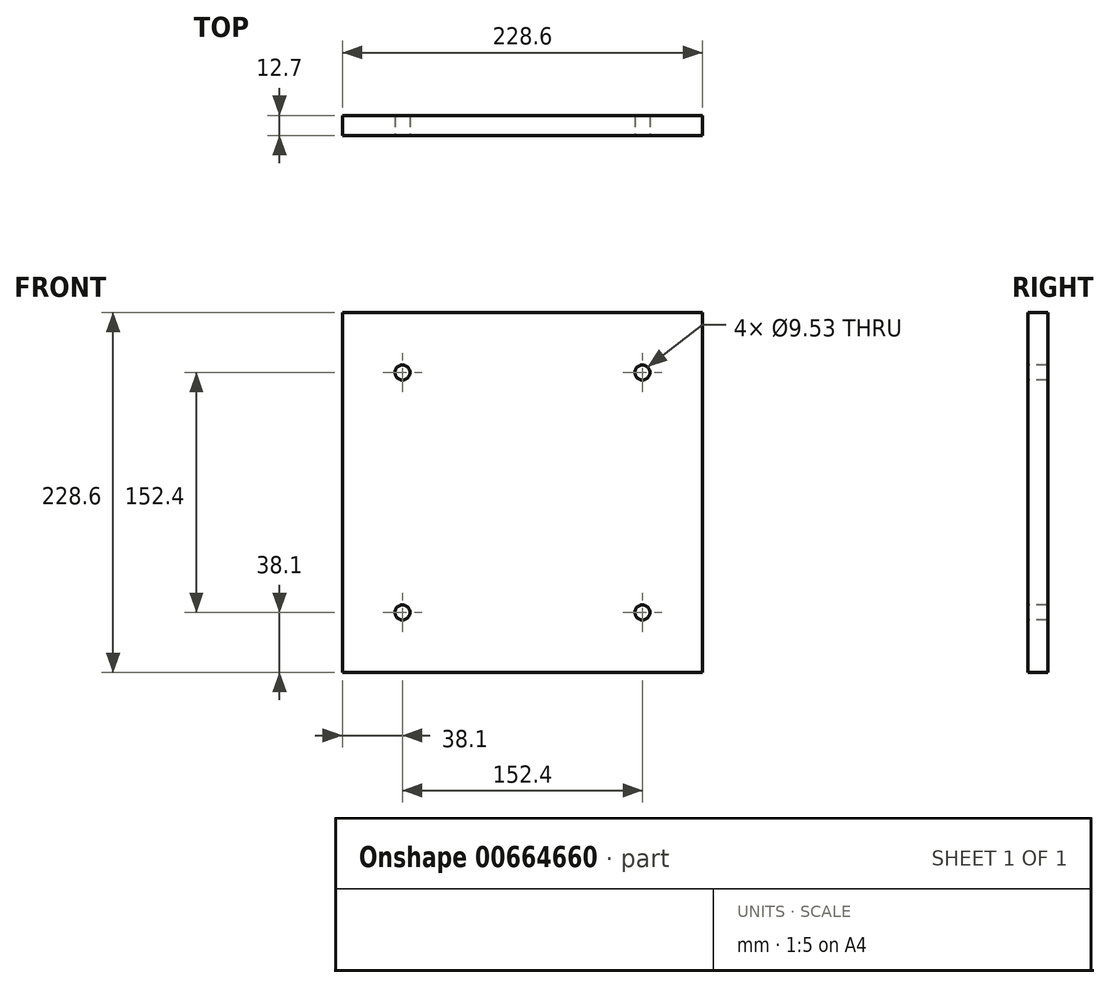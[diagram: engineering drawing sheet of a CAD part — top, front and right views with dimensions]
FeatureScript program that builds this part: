
annotation { "Feature Type Name" : "Feature", "Feature Type Description" : "" }
export const myFeature = defineFeature(function(context is Context, id is Id, definition is map)
    precondition{}
    {
        {
            var Q0;
            Q0=qCreatedBy(makeId("Front.planeOp"),FACE);
            var sketch = newSketch(context, id + "F0", { "sketchPlane" : qUnion([Q0])});
            skLineSegment(sketch, "E0.bottom", {"start": v(114.3, 114.3) * mm, "end": v(-114.3, 114.3) * mm});
            skLineSegment(sketch, "E0.top", {"start": v(114.3, -114.3) * mm, "end": v(-114.3, -114.3) * mm});
            skLineSegment(sketch, "E0.left", {"start": v(114.3, 114.3) * mm, "end": v(114.3, -114.3) * mm});
            skLineSegment(sketch, "E0.right", {"start": v(-114.3, 114.3) * mm, "end": v(-114.3, -114.3) * mm});
            skPoint(sketch, "E0.middle", {"position": v(0, 0) * mm});
            skSolve(sketch);
        }
        {
            var Q0;
            Q0 = qSketchRegion(id + "F0", true);
            extrude(context, id + "F1", {"entities" : qUnion([Q0]), "depth" : 12.7 * mm, "offsetDistance" : 25.4 * mm});
        }
        {
            var Q0;
            Q0=makeQuery(id+"F1.opExtrude","CAP_FACE",FACE,{"disambiguationData":[OSD([sQuery(id+"F0.wireOp",EDGE,"E0.bottom"),sQuery(id+"F0.wireOp",EDGE,"E0.top"),sQuery(id+"F0.wireOp",EDGE,"E0.left"),sQuery(id+"F0.wireOp",EDGE,"E0.right")])],"isStart":false});
            var sketch = newSketch(context, id + "F2", { "sketchPlane" : qUnion([Q0])});
            skLineSegment(sketch, "E1.bottom", {"start": v(76.2, 76.2) * mm, "end": v(-76.2, 76.2) * mm});
            skLineSegment(sketch, "E1.top", {"start": v(76.2, -76.2) * mm, "end": v(-76.2, -76.2) * mm});
            skLineSegment(sketch, "E1.left", {"start": v(76.2, 76.2) * mm, "end": v(76.2, -76.2) * mm});
            skLineSegment(sketch, "E1.right", {"start": v(-76.2, 76.2) * mm, "end": v(-76.2, -76.2) * mm});
            skPoint(sketch, "E1.middle", {"position": v(0, 0) * mm});
            skSolve(sketch);
        }
        {
            var Q0;
            Q0=sQuery(id+"F2.wireOp",VERTEX,"E1.right.start");
            var Q1;
            Q1=sQuery(id+"F2.wireOp",VERTEX,"E1.left.start");
            var Q2;
            Q2=sQuery(id+"F2.wireOp",VERTEX,"E1.left.end");
            var Q3;
            Q3=sQuery(id+"F2.wireOp",VERTEX,"E1.top.end");
            var Q4;
            Q4=makeQuery(id+"F1.opExtrude","SWEPT_BODY",BODY,{"disambiguationData":[OSD([sQuery(id+"F0.wireOp",EDGE,"E0.bottom"),sQuery(id+"F0.wireOp",EDGE,"E0.top"),sQuery(id+"F0.wireOp",EDGE,"E0.left"),sQuery(id+"F0.wireOp",EDGE,"E0.right")])]});
            hole(context, id + "F3", {"style" : HoleStyle.SIMPLE, "endStyle" : HoleEndStyle.THROUGH, "holeDiameter" : 9.52 * mm, "majorDiameter" : 6.35 * mm, "isTappedThrough" : true, "tappedDepth" : 12.7 * mm, "tapClearance" : 3, "startFromSketch" : true, "locations" : qUnion([Q0, Q1, Q2, Q3]), "scope" : qUnion([Q4])});
        }
    });
